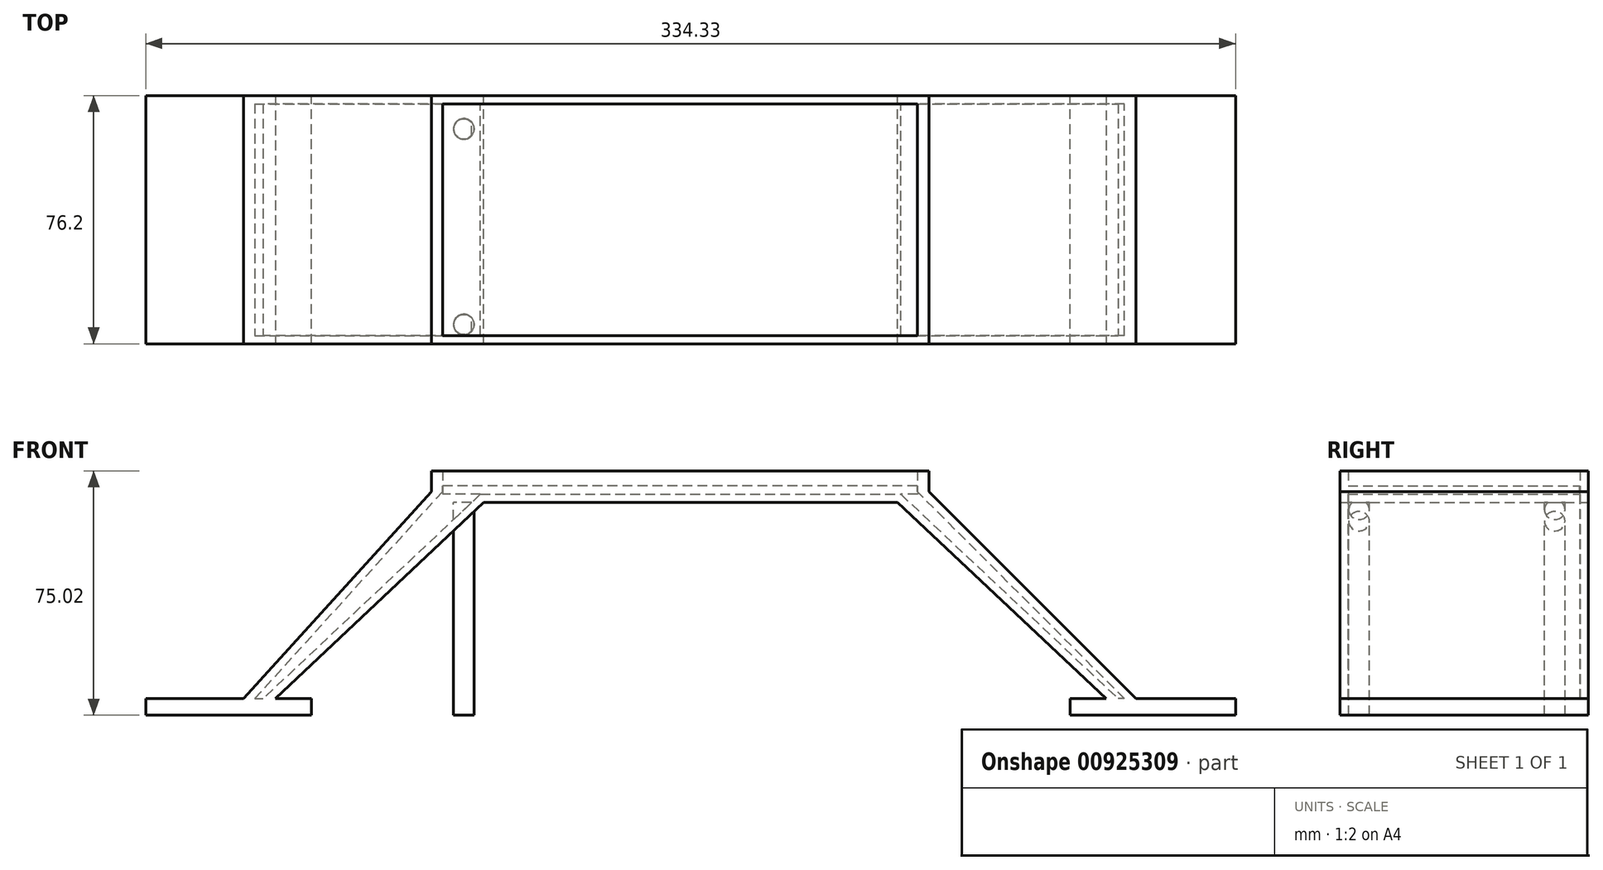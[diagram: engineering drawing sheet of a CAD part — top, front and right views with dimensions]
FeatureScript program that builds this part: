
annotation { "Feature Type Name" : "Feature", "Feature Type Description" : "" }
export const myFeature = defineFeature(function(context is Context, id is Id, definition is map)
    precondition{}
    {
        {
            var Q0;
            Q0=qCreatedBy(makeId("Front.planeOp"),FACE);
            var sketch = newSketch(context, id + "F0", { "sketchPlane" : qUnion([Q0])});
            skLineSegment(sketch, "E0", {"start": v(-63.37, 0) * mm, "end": v(63.63, 0) * mm});
            skLineSegment(sketch, "E1", {"start": v(-79.41, 3.4) * mm, "end": v(73.23, 3.4) * mm});
            skLineSegment(sketch, "E2", {"start": v(-63.37, 0) * mm, "end": v(-132.74, -65.27) * mm});
            skLineSegment(sketch, "E3", {"start": v(-132.74, -65.27) * mm, "end": v(-141.63, -65.27) * mm});
            skLineSegment(sketch, "E4", {"start": v(-141.63, -65.27) * mm, "end": v(-79.41, 3.4) * mm});
            skLineSegment(sketch, "E5", {"start": v(63.63, 0) * mm, "end": v(133, -65.27) * mm});
            skLineSegment(sketch, "E6", {"start": v(133, -65.27) * mm, "end": v(141.9, -65.27) * mm});
            skLineSegment(sketch, "E7", {"start": v(141.9, -65.27) * mm, "end": v(73.23, 3.4) * mm});
            skLineSegment(sketch, "E8", {"start": v(-132.74, -65.27) * mm, "end": v(133, -65.27) * mm});
            skSolve(sketch);
        }
        {
            var Q0;
            Q0=makeQuery(id+"F0.imprint","IMPRINT",FACE,{"disambiguationData":[TD([[makeQuery(id+"F0.imprint","IMPRINT",EDGE,{"derivedFrom":sQuery(id+"F0.wireOp",EDGE,"E0")}),1.0]])]});
            extrude(context, id + "F1", {"entities" : qUnion([Q0]), "depth" : 38.1 * mm, "offsetDistance" : 25.4 * mm, "hasSecondDirection" : true, "secondDirectionOppositeDirection" : true, "secondDirectionDepth" : 38.1 * mm});
        }
        {
            var Q0;
            Q0=makeQuery(id+"F1.opExtrude","SWEPT_FACE",FACE,{"disambiguationData":[OSD([sQuery(id+"F0.wireOp",EDGE,"E1")])]});
            shell(context, id + "F2", {"entities" : qUnion([Q0]), "thickness" : 2.54 * mm});
        }
        {
            var Q0;
            Q0=makeQuery(id+"F1.opExtrude","SWEPT_FACE",FACE,{"disambiguationData":[OSD([sQuery(id+"F0.wireOp",EDGE,"E0")])]});
            var sketch = newSketch(context, id + "F3", { "sketchPlane" : qUnion([Q0])});
            skCircle(sketch, "E9", {"center": v(-69.44, 32.18) * mm, "radius": 3.18 * mm});
            skLineSegment(sketch, "E10", {"start": v(0, 38.1) * mm, "end": v(0, -38.1) * mm, "construction": true});
            skCircle(sketch, "E11", {"center": v(-69.44, -27.84) * mm, "radius": 3.18 * mm});
            skCircle(sketch, "E12.MirrorC", {"center": v(69.44, 32.18) * mm, "radius": 3.18 * mm});
            skCircle(sketch, "E13.MirrorC", {"center": v(69.44, -27.84) * mm, "radius": 3.18 * mm});
            skLineSegment(sketch, "E14", {"start": v(-69.44, 32.18) * mm, "end": v(-69.44, -27.84) * mm, "construction": true});
            skSolve(sketch);
        }
        {
            var Q0;
            Q0=makeQuery(id+"F3.imprint","IMPRINT",FACE,{"disambiguationData":[TD([[makeQuery(id+"F3.imprint","IMPRINT",EDGE,{"derivedFrom":sQuery(id+"F3.wireOp",EDGE,"E9")}),1.0]])]});
            var Q1;
            Q1=makeQuery(id+"F3.imprint","IMPRINT",FACE,{"disambiguationData":[TD([[makeQuery(id+"F3.imprint","IMPRINT",EDGE,{"derivedFrom":sQuery(id+"F3.wireOp",EDGE,"E12.MirrorC")}),-1.0]])]});
            var Q2;
            Q2=makeQuery(id+"F3.imprint","IMPRINT",FACE,{"disambiguationData":[TD([[makeQuery(id+"F3.imprint","IMPRINT",EDGE,{"derivedFrom":sQuery(id+"F3.wireOp",EDGE,"E13.MirrorC")}),-1.0]])]});
            var Q3;
            Q3=makeQuery(id+"F3.imprint","IMPRINT",FACE,{"disambiguationData":[TD([[makeQuery(id+"F3.imprint","IMPRINT",EDGE,{"derivedFrom":sQuery(id+"F3.wireOp",EDGE,"E11")}),1.0]])]});
            extrude(context, id + "F4", {"entities" : qUnion([Q0, Q1, Q2, Q3]), "operationType" : NewBodyOperationType.ADD, "depth" : 65.25 * mm, "offsetDistance" : 25.4 * mm});
        }
        {
            var Q0;
            Q0=makeQuery(id+"F1.opExtrude","SWEPT_FACE",FACE,{"disambiguationData":[OSD([sQuery(id+"F0.wireOp",EDGE,"E1")])]});
            extrude(context, id + "F5", {"entities" : qUnion([Q0]), "operationType" : NewBodyOperationType.ADD, "depth" : 6.35 * mm, "offsetDistance" : 25.4 * mm});
        }
        {
            var Q0;
            Q0=makeQuery(id+"F2.opShell","OFFSET_FACE",FACE,{"disambiguationData":[OSD([sQuery(id+"F0.wireOp",EDGE,"E0")])]});
            var sketch = newSketch(context, id + "F6", { "sketchPlane" : qUnion([Q0])});
            skLineSegment(sketch, "E15.bottom", {"start": v(69.76, 35.5) * mm, "end": v(-76.02, 35.5) * mm});
            skLineSegment(sketch, "E15.top", {"start": v(69.76, -35.56) * mm, "end": v(-76.02, -35.56) * mm});
            skLineSegment(sketch, "E15.left", {"start": v(69.76, 35.5) * mm, "end": v(69.76, -35.56) * mm});
            skLineSegment(sketch, "E15.right", {"start": v(-76.02, 35.5) * mm, "end": v(-76.02, -35.56) * mm});
            skSolve(sketch);
        }
        {
            var Q0;
            {var subQ0=sQuery(id+"F6.wireOp",EDGE,"E15.left");Q0=makeQuery(id+"F6.imprint","IMPRINT",FACE,{"disambiguationData":[TD([[makeQuery(id+"F6.imprint","IMPRINT",EDGE,{"derivedFrom":subQ0}),-1.0]])]});}
            var Q1;
            {var subQ0=sQuery(id+"F6.wireOp",EDGE,"E15.bottom");var subQ1=sQuery(id+"F0.wireOp",EDGE,"E0");var subQ2=makeQuery(id+"F2.opShell","OFFSET_EDGE",EDGE,{"disambiguationData":[OSD([subQ1,sQuery(id+"F0.wireOp",EDGE,"E5")])]});var subQ3=makeQuery(id+"F6.imprint","INTERSECT",VERTEX,{"derivedFrom":[subQ2,subQ0]});Q1=makeQuery(id+"F6.imprint","IMPRINT",FACE,{"disambiguationData":[TD([[makeQuery(id+"F6.imprint","IMPRINT",EDGE,{"disambiguationData":[TD([[subQ3,-1.0]])],"derivedFrom":subQ0}),1.0]])]});}
            var Q2;
            {var subQ0=sQuery(id+"F6.wireOp",EDGE,"E15.right");Q2=makeQuery(id+"F6.imprint","IMPRINT",FACE,{"disambiguationData":[TD([[makeQuery(id+"F6.imprint","IMPRINT",EDGE,{"derivedFrom":subQ0}),1.0]])]});}
            extrude(context, id + "F7", {"entities" : qUnion([Q0, Q1, Q2]), "operationType" : NewBodyOperationType.ADD, "depth" : 2.54 * mm, "offsetDistance" : 25.4 * mm});
        }
        {
            var Q0;
            Q0=makeQuery(id+"F1.opExtrude","SWEPT_FACE",FACE,{"disambiguationData":[OSD([sQuery(id+"F0.wireOp",EDGE,"E6")])]});
            var Q1;
            Q1=makeQuery(id+"F1.opExtrude","SWEPT_FACE",FACE,{"disambiguationData":[OSD([sQuery(id+"F0.wireOp",EDGE,"E3")])]});
            extrude(context, id + "F8", {"entities" : qUnion([Q0, Q1]), "operationType" : NewBodyOperationType.ADD, "oppositeDirection" : true, "depth" : 5.08 * mm, "offsetDistance" : 25.4 * mm});
        }
        {
            var Q0;
            Q0=makeQuery(id+"F8.opExtrude","SWEPT_FACE",FACE,{"disambiguationData":[OSD([sQuery(id+"F0.wireOp",EDGE,"E6"),sQuery(id+"F0.wireOp",EDGE,"E7")])]});
            var Q1;
            Q1=makeQuery(id+"F8.opExtrude","SWEPT_FACE",FACE,{"disambiguationData":[OSD([sQuery(id+"F0.wireOp",EDGE,"E3"),sQuery(id+"F0.wireOp",EDGE,"E4")])]});
            extrude(context, id + "F9", {"entities" : qUnion([Q0, Q1]), "operationType" : NewBodyOperationType.ADD, "depth" : 25.4 * mm, "offsetDistance" : 25.4 * mm, "hasSecondDirection" : true, "secondDirectionOppositeDirection" : true, "secondDirectionDepth" : 25.4 * mm});
        }
    });
